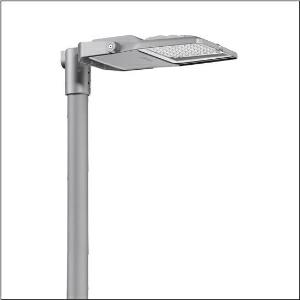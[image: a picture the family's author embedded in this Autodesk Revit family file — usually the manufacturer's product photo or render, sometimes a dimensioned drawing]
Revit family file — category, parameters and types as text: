
# Revit family: floodlight_fl_21_iq_mini___pl64_5xa7771c4e3a_84b6
name_source: partatom
category: Lighting Fixtures
units: mm (PartAtom-declared; Revit-internal decimal feet)

## family parameters
Cut with Voids When Loaded = No
Host = Face
Light Source = No
Part Type = Normal
Room Calculation Point = No
Round Connector Dimension = Use Diameter
Shared = No

## types (1)
- --- (1 x LED, 12280 lm, 87.2 W, 4000K)
    Apparent Load = 87 VA
    CIE Flux Codes = 28 80 98 100 100
    Color Rendering = 70
    Color Temperature = 4000K
    Default Elevation = 1800 mm
    Description = Floodlight FL 21 iQ mini, floodlight, primary light control with lens, of PMMA, primary optical cover: protective disc, of toughened safety glass, transparent, light distribution: PL64, light emission: direct distribution, installation type: surface-mounted, LED, High Power LED, rated luminous flux: 12.280lm, luminous efficacy: 141lm/W, light colour: 740, colour temperature: 4000K, control: Auto-Match, Temp-Guard, Lumen-Switch, Night-Set, Smart-Wire, Light-Fading, Desk-Remote (wireless, voltage-free reading and setting of iQ features in the workshop via application-optimized NFC function/RFID function), optimised constant luminous flux control (CLO 2.0), with terminal, 6-pole, mains connection: 220..240V, AC, 50/60Hz, start of lifetime: 87W, end of service life: 92W, reduction: 40W, luminaire housing, of diecast aluminium, powder-coated, Siteco® metallic grey (DB 702S), corrosivity category C5 mid according to DIN EN ISO 12944, sealing non-destructively replaceable, please order mast flange separately, mast bracket, of steel, galvanised, powder-coated, Siteco® metallic grey (DB 702S), protection rating (complete): IP66, insulation class (complete): insulation class II (safety insulation), certification: CE, ENEC, VDE, protection symbol: D, impact resistance: IK08, permissible operating ambient temperature: -40..+40°C, permissible operating ambient temperature for outdoor applications: -40..+50°C, standard: DIN EN 12944, LABS conformity tested according to VDMA 24364:2018-05, packaging unit: 1 piece

Light Distribution: PL64
    Height = 70 mm
    Lamp = 1 x LED
    Lamp Light Flux = 12280 lm
    Lamp Power = 87.2 W
    Lamp count = 1
    Length = 485 mm
    Luminous efficacy = 141 lm/W
    Manufacturer = Siteco
    ModVariant = No
    Model = 5XA7771C4E3A
    Number of Poles = 1
    OnlyDefault = Yes
    Power Factor = 1
    Product Name = Floodlight FL 21 iQ mini | PL64
    Product group = floodlight | pylon annexe
    ProductGroupID = 6200
    Protection Class = Protection class II
    Protection Degree = IP 66
    RLX_Detail_Level = 1
    RLX_Emergency_Light_Flux = 0 lm
    RLX_Emergency_Type = 0
    RLX_Emergency_Type_DB = No
    RlxData = <blob elided: 101281 chars, md5=ce433b96>
    Socket = socket
    Standby Power = 0 W
    System Light Flux = 12280 lm
    System Power = 87 W
    Type Comments = factory setting: luminous flux: 100 % | dim-lin: 254 | 456 mA
    Type Image = l_1007125.jpg
    URL = http://relux.com
    VarID = @adj_098805
    Voltage = 0 V
    Weight = 0.00 kg
    Width = 337 mm

## geometry (parser evidence)
native form markers: Blend x4, Sweep x12
no freeform markers — native parametric forms only
